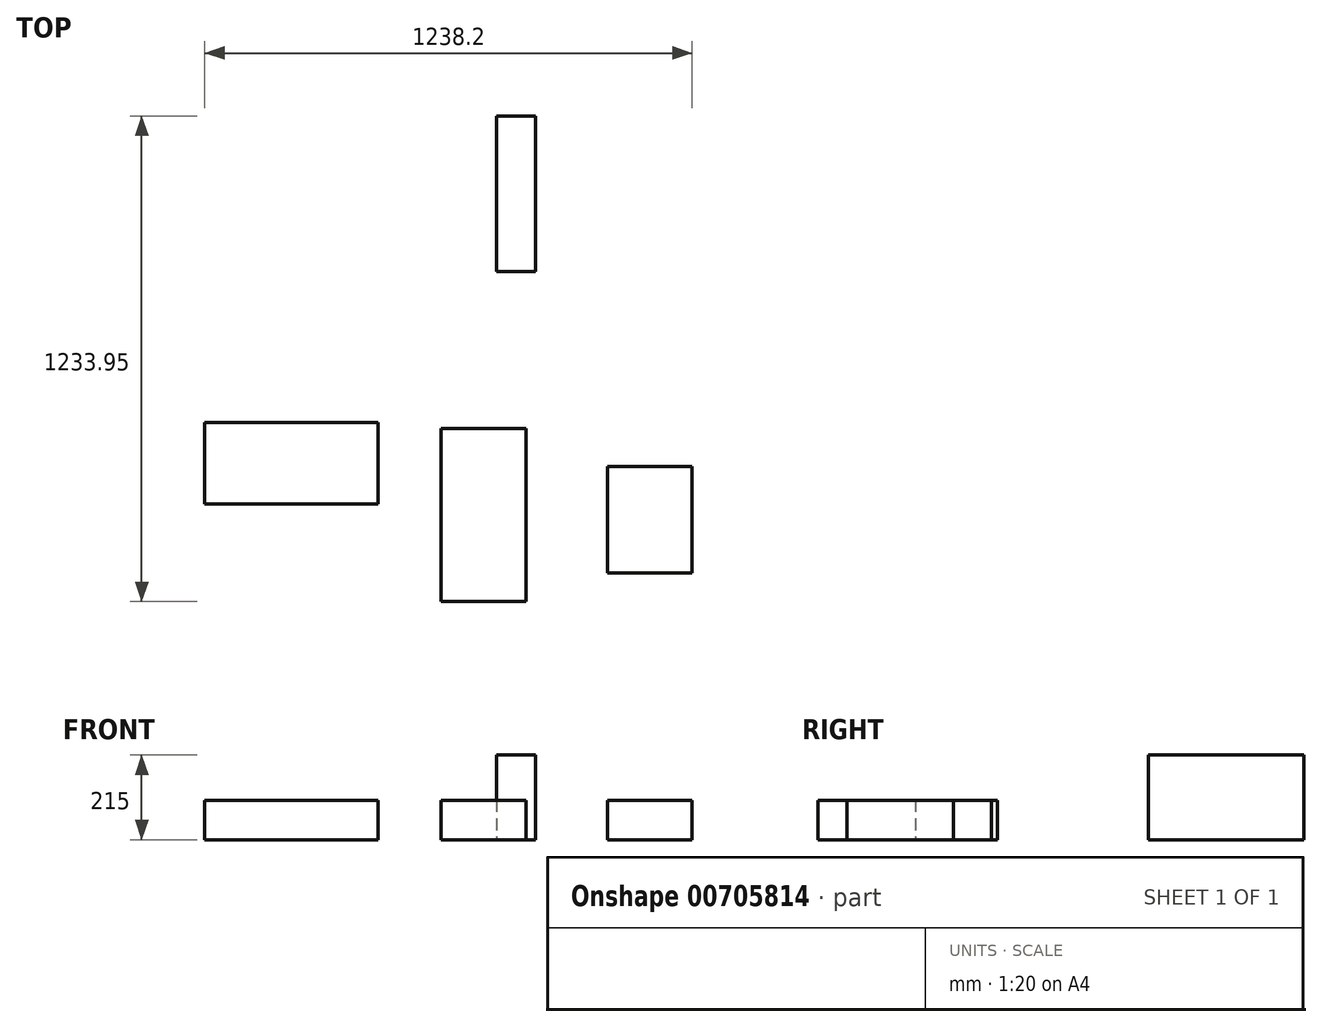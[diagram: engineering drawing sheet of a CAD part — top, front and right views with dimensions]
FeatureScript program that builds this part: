
annotation { "Feature Type Name" : "Feature", "Feature Type Description" : "" }
export const myFeature = defineFeature(function(context is Context, id is Id, definition is map)
    precondition{}
    {
        {
            var Q0;
            Q0=qCreatedBy(makeId("Top.planeOp"),FACE);
            var sketch = newSketch(context, id + "F0", { "sketchPlane" : qUnion([Q0])});
            skLineSegment(sketch, "E0.bottom", {"start": v(-32.16, -29.58) * mm, "end": v(182.84, -29.58) * mm});
            skLineSegment(sketch, "E0.top", {"start": v(-32.16, 410.42) * mm, "end": v(182.84, 410.42) * mm});
            skLineSegment(sketch, "E0.left", {"start": v(-32.16, -29.58) * mm, "end": v(-32.16, 410.42) * mm});
            skLineSegment(sketch, "E0.right", {"start": v(182.84, -29.58) * mm, "end": v(182.84, 410.42) * mm});
            skSolve(sketch);
        }
        {
            var Q0;
            Q0=makeQuery(id+"F0.imprint","IMPRINT",FACE,{"disambiguationData":[TD([[makeQuery(id+"F0.imprint","IMPRINT",EDGE,{"derivedFrom":sQuery(id+"F0.wireOp",EDGE,"E0.bottom")}),1.0]])]});
            extrude(context, id + "F1", {"entities" : qUnion([Q0]), "depth" : 100 * mm, "offsetDistance" : 25 * mm});
        }
        {
            var Q0;
            Q0=qCreatedBy(makeId("Top.planeOp"),FACE);
            var sketch = newSketch(context, id + "F2", { "sketchPlane" : qUnion([Q0])});
            skLineSegment(sketch, "E1.bottom", {"start": v(390.28, 43.5) * mm, "end": v(605.28, 43.5) * mm});
            skLineSegment(sketch, "E1.top", {"start": v(390.28, 313.5) * mm, "end": v(605.28, 313.5) * mm});
            skLineSegment(sketch, "E1.left", {"start": v(390.28, 43.5) * mm, "end": v(390.28, 313.5) * mm});
            skLineSegment(sketch, "E1.right", {"start": v(605.28, 43.5) * mm, "end": v(605.28, 313.5) * mm});
            skSolve(sketch);
        }
        {
            var Q0;
            Q0=makeQuery(id+"F2.imprint","IMPRINT",FACE,{"disambiguationData":[TD([[makeQuery(id+"F2.imprint","IMPRINT",EDGE,{"derivedFrom":sQuery(id+"F2.wireOp",EDGE,"E1.bottom")}),1.0]])]});
            extrude(context, id + "F3", {"entities" : qUnion([Q0]), "depth" : 100 * mm, "offsetDistance" : 25 * mm});
        }
        {
            var Q0;
            Q0=qCreatedBy(makeId("Top.planeOp"),FACE);
            var sketch = newSketch(context, id + "F4", { "sketchPlane" : qUnion([Q0])});
            skLineSegment(sketch, "E2.bottom", {"start": v(-632.92, 217.82) * mm, "end": v(-192.92, 217.82) * mm});
            skLineSegment(sketch, "E2.top", {"start": v(-632.92, 425.32) * mm, "end": v(-192.92, 425.32) * mm});
            skLineSegment(sketch, "E2.left", {"start": v(-632.92, 217.82) * mm, "end": v(-632.92, 425.32) * mm});
            skLineSegment(sketch, "E2.right", {"start": v(-192.92, 217.82) * mm, "end": v(-192.92, 425.32) * mm});
            skSolve(sketch);
        }
        {
            var Q0;
            Q0=makeQuery(id+"F4.imprint","IMPRINT",FACE,{"disambiguationData":[TD([[makeQuery(id+"F4.imprint","IMPRINT",EDGE,{"derivedFrom":sQuery(id+"F4.wireOp",EDGE,"E2.bottom")}),1.0]])]});
            extrude(context, id + "F5", {"entities" : qUnion([Q0]), "depth" : 100 * mm, "offsetDistance" : 25 * mm});
        }
        {
            var Q0;
            Q0=qCreatedBy(makeId("Top.planeOp"),FACE);
            var sketch = newSketch(context, id + "F6", { "sketchPlane" : qUnion([Q0])});
            skLineSegment(sketch, "E3.bottom", {"start": v(107.65, 809.37) * mm, "end": v(207.65, 809.37) * mm});
            skLineSegment(sketch, "E3.top", {"start": v(107.65, 1204.37) * mm, "end": v(207.65, 1204.37) * mm});
            skLineSegment(sketch, "E3.left", {"start": v(107.65, 809.37) * mm, "end": v(107.65, 1204.37) * mm});
            skLineSegment(sketch, "E3.right", {"start": v(207.65, 809.37) * mm, "end": v(207.65, 1204.37) * mm});
            skSolve(sketch);
        }
        {
            var Q0;
            Q0=makeQuery(id+"F6.imprint","IMPRINT",FACE,{"disambiguationData":[TD([[makeQuery(id+"F6.imprint","IMPRINT",EDGE,{"derivedFrom":sQuery(id+"F6.wireOp",EDGE,"E3.bottom")}),1.0]])]});
            extrude(context, id + "F7", {"entities" : qUnion([Q0]), "depth" : 215 * mm, "offsetDistance" : 25 * mm});
        }
    });
